# Revit family: 40_703510001_Fluxometro Sanitario Sensor Tru Flush
name_source: partatom
category: Aparatos sanitarios
revit_build: Autodesk Revit 2018 (Build: 20170223_1515(x64)
units: mm (PartAtom-declared; Revit-internal decimal feet)

## family parameters
Anfitrión = Muro
Compartido = No
Corte con vacíos al cargar = No
Cota de conector redondo = Diámetro de uso
Número OmniClass = 23.45.05.14.99
Punto de cálculo de habitación = No
Siempre vertical = Sí
Tipo de pieza = Normal
Título OmniClass = Other Sanitary Washing Plumbing Fixtures

## types (1)
- Tipo 1
    Accionamiento = Sin Contacto
    Consumo de Agua = 4.8 Litros por descarga
    Cumple ADA = SI
    Cumple EDGE = SI
    Cumple LEED = SI
    Diametro conexión = 1 ½” NPT
    Garantía = 3 años
    HET = SI
    Marca = SLOAN VALVE
    Material = Latón
    Nombre = Fluxometro Sanitario Sensor Tru Flush
    Presión Máxima = 80
    Presión Mínima = 30
    Referencia = 703510001
    Tipo = Válvula descarga
    Tráfico = Institucional Alto tráfico
    URL = https://www.corona.co
    Vida Util (ciclos) = 150000
